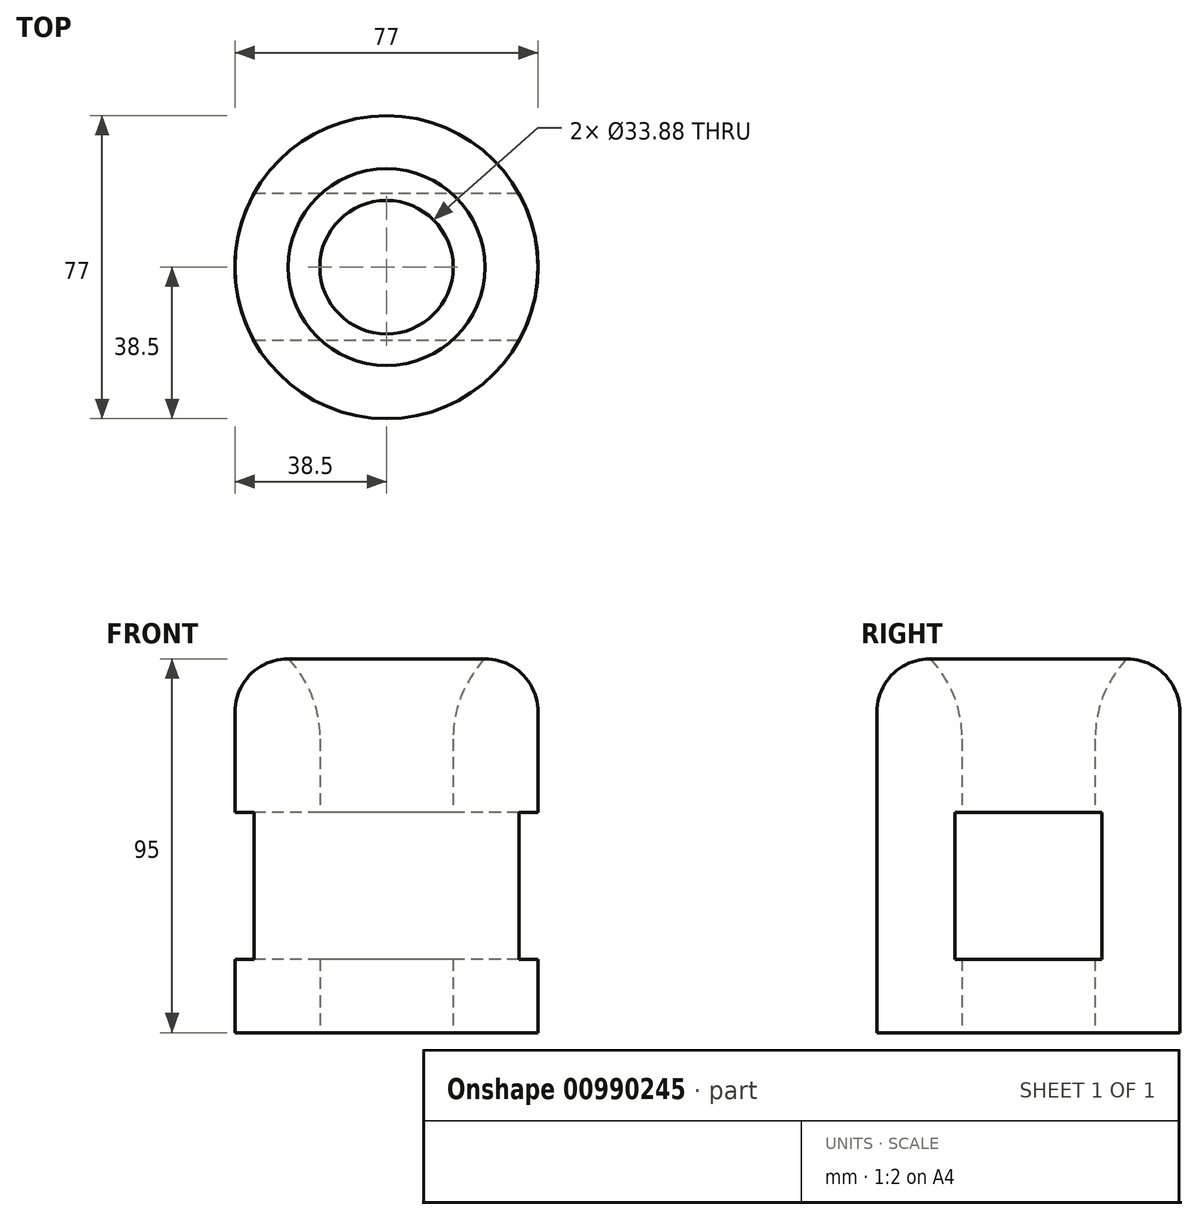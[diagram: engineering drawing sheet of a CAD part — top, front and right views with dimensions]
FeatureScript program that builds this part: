
annotation { "Feature Type Name" : "Feature", "Feature Type Description" : "" }
export const myFeature = defineFeature(function(context is Context, id is Id, definition is map)
    precondition{}
    {
        {
            var Q0;
            Q0=qCreatedBy(makeId("Top.planeOp"),FACE);
            var sketch = newSketch(context, id + "F0", { "sketchPlane" : qUnion([Q0])});
            skCircle(sketch, "E0", {"center": v(0, 0) * mm, "radius": 38.5 * mm});
            skCircle(sketch, "E1", {"center": v(0, 0) * mm, "radius": 16.94 * mm});
            skSolve(sketch);
        }
        {
            var Q0;
            Q0=makeQuery(id+"F0.imprint","IMPRINT",FACE,{"disambiguationData":[TD([[makeQuery(id+"F0.imprint","IMPRINT",EDGE,{"derivedFrom":sQuery(id+"F0.wireOp",EDGE,"E0")}),1.0]])]});
            extrude(context, id + "F1", {"entities" : qUnion([Q0]), "depth" : 95 * mm, "offsetDistance" : 25 * mm});
        }
        {
            var Q0;
            Q0=qCreatedBy(makeId("Top.planeOp"),FACE);
            cPlane(context, id + "F2", {"entities" : qUnion([Q0]), "cplaneType" : CPlaneType.OFFSET, "offset" : 37.3 * mm, "width" : 150 * mm, "height" : 150 * mm});
        }
        {
            var Q0;
            Q0=qCreatedBy(id+"F2.planeOp",FACE);
            var sketch = newSketch(context, id + "F3", { "sketchPlane" : qUnion([Q0])});
            skCircle(sketch, "E2.0", {"center": v(0, 0) * mm, "radius": 38.5 * mm});
            skLineSegment(sketch, "E3", {"start": v(-38.5, 0) * mm, "end": v(-38.5, 45.13) * mm});
            skSolve(sketch);
        }
        {
            var Q0;
            Q0=sQuery(id+"F3.wireOp",EDGE,"E3");
            cPlane(context, id + "F4", {"entities" : qUnion([Q0]), "cplaneType" : CPlaneType.LINE_ANGLE, "offset" : 25 * mm, "angle" : 90 * degree, "width" : 150 * mm, "height" : 150 * mm});
        }
        {
            var Q0;
            Q0=qCreatedBy(id+"F4.planeOp",FACE);
            var sketch = newSketch(context, id + "F5", { "sketchPlane" : qUnion([Q0])});
            skPoint(sketch, "E4.0", {"position": v(0, 37.3) * mm});
            skLineSegment(sketch, "E5.bottom", {"start": v(-18.64, 18.67) * mm, "end": v(18.64, 18.67) * mm});
            skLineSegment(sketch, "E5.top", {"start": v(-18.64, 55.93) * mm, "end": v(18.64, 55.93) * mm});
            skLineSegment(sketch, "E5.left", {"start": v(-18.64, 18.67) * mm, "end": v(-18.64, 55.93) * mm});
            skLineSegment(sketch, "E5.right", {"start": v(18.64, 18.67) * mm, "end": v(18.64, 55.93) * mm});
            skSolve(sketch);
        }
        {
            var Q0;
            Q0=makeQuery(id+"F5.imprint","IMPRINT",FACE,{"disambiguationData":[TD([[makeQuery(id+"F5.imprint","IMPRINT",EDGE,{"derivedFrom":sQuery(id+"F5.wireOp",EDGE,"E5.bottom")}),1.0]])]});
            extrude(context, id + "F6", {"entities" : qUnion([Q0]), "operationType" : NewBodyOperationType.REMOVE, "depth" : 100 * mm, "offsetDistance" : 25 * mm});
        }
        {
            var Q0;
            Q0=makeQuery(id+"F1.opExtrude","CAP_EDGE",EDGE,{"disambiguationData":[OSD([sQuery(id+"F0.wireOp",EDGE,"E0")])],"isStart":false});
            fillet(context, id + "F7", {"entities" : qUnion([Q0]), "radius" : 13.52 * mm, "tangentPropagation" : true, "allowEdgeOverflow" : false});
        }
        {
            var Q0;
            Q0=makeQuery(id+"F1.opExtrude","CAP_EDGE",EDGE,{"disambiguationData":[OSD([sQuery(id+"F0.wireOp",EDGE,"E1")])],"isStart":false});
            fillet(context, id + "F8", {"entities" : qUnion([Q0]), "radius" : 29.85 * mm, "tangentPropagation" : true, "allowEdgeOverflow" : false});
        }
    });
